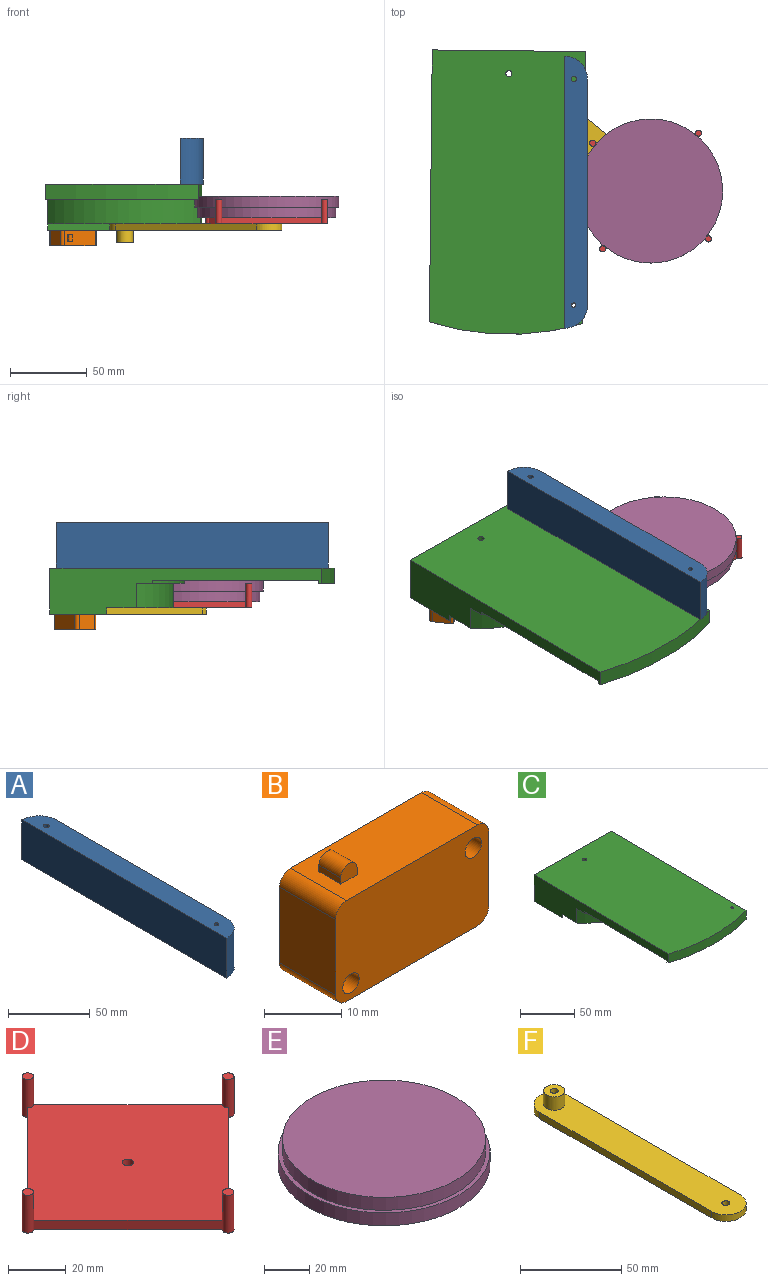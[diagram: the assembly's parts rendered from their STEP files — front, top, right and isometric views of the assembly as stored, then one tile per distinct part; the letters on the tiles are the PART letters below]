
ASSEMBLY  parts=6 mates=5
PART A: 8 faces, bbox 15x177.5x30 mm
  f0: cylinder r=15mm len=30mm, axis (0,0,-1), area 706.9mm2, adj f1,f4,f6,f7
  f1: plane 147.52x30mm, normal (1,0,0), area 4425.6mm2, adj f0,f2,f6,f7
  f2: cylinder r=15mm len=30mm, axis (0,0,-1), area 706.9mm2, adj f1,f4,f6,f7
  f3: cylinder r=1.5mm len=30mm, axis (0,0,-1), area 282.7mm2, adj f6,f7
  f4: plane 177.52x30mm, normal (-1,0,0), area 5325.6mm2, adj f0,f2,f6,f7
  f5: cylinder r=1.76mm len=30mm, axis (0,0,-1), area 331mm2, adj f6,f7
  f6: plane 177.52x15mm, normal (0,0,1), area 2549.5mm2, adj f0,f1,f2,f3,f4,f5
  f7: plane 177.52x15mm, normal (0,0,-1), area 2549.5mm2, adj f0,f1,f2,f3,f4,f5
PART B: 17 faces, bbox 28x10.3x18.5 mm
  f0: plane 24x10.3mm, normal (0,0,1), area 235.2mm2, adj f6,f7,f8,f9,f11,f12,f13,f16
  f1: plane 12x10.3mm, normal (-1,0,0), area 123.6mm2, adj f6,f7,f13,f14
  f2: plane 24x10.3mm, normal (0,0,-1), area 247.2mm2, adj f6,f7,f14,f15
  f3: cylinder r=1.5mm len=10.3mm, axis (0,1,0), area 97.1mm2, adj f6,f7
  f4: plane 12x10.3mm, normal (1,0,0), area 123.6mm2, adj f6,f7,f15,f16
  f5: cylinder r=1.5mm len=10.3mm, axis (0,1,0), area 97.1mm2, adj f6,f7
  f6: plane 28x16mm, normal (0,-1,0), area 430.4mm2, adj f0,f1,f2,f3,f4,f5,f13,f14
  f7: plane 28x16mm, normal (0,1,0), area 430.4mm2, adj f0,f1,f2,f3,f4,f5,f13,f14
  f8: plane 4x1mm, normal (-1,0,0), area 4mm2, adj f0,f10,f11,f12
  f9: plane 4x1mm, normal (1,0,0), area 4mm2, adj f0,f10,f11,f12
  f10: cylinder r=1.5mm len=4mm, axis (0,1,0), area 18.8mm2, adj f8,f9,f11,f12
  f11: plane 3x2.5mm, normal (0,-1,0), area 6.5mm2, adj f0,f8,f9,f10
  f12: plane 3x2.5mm, normal (0,1,0), area 6.5mm2, adj f0,f8,f9,f10
  f13: cylinder r=2mm len=10.3mm, axis (0,-1,0), area 32.4mm2, adj f0,f1,f6,f7
  f14: cylinder r=2mm len=10.3mm, axis (0,1,0), area 32.4mm2, adj f1,f2,f6,f7
  f15: cylinder r=2mm len=10.3mm, axis (0,-1,0), area 32.4mm2, adj f2,f4,f6,f7
  f16: cylinder r=2mm len=10.3mm, axis (0,1,0), area 32.4mm2, adj f0,f4,f6,f7
PART C: 18 faces, bbox 101.8x185.5x30 mm
  f0: plane 99.99x30mm, normal (0.01,1,0), area 3000mm2, adj f1,f3,f7,f17
  f1: plane 177.42x30mm, normal (-1,0.01,0), area 2606.2mm2, adj f0,f2,f6,f7,f8,f9,f10,f11
  f2: cylinder r=170mm len=99.99mm, axis (0,0,1), area 1015mm2, adj f1,f3,f7,f13
  f3: plane 177.52x30mm, normal (1,-0.01,0), area 2607.5mm2, adj f0,f2,f6,f7,f8,f9,f10,f11
  f4: cylinder r=2mm len=26mm, axis (0,0,1), area 326.7mm2, adj f7,f9
  f5: cylinder r=1.25mm len=8mm, axis (0,0,1), area 62.8mm2, adj f6,f7
  f6: plane 116.87x101.12mm, normal (0,0,-1), area 9973.8mm2, adj f1,f3,f5,f10,f12
  f7: plane 185.52x101.84mm, normal (0,0,1), area 18234.1mm2, adj f0,f1,f2,f3,f4,f5
  f8: cylinder r=65mm len=99.99mm, axis (0,0,1), area 1825.5mm2, adj f1,f3,f9,f11
  f9: plane 100.21x75.55mm, normal (0,0,-1), area 5312.2mm2, adj f1,f3,f4,f8,f14,f15,f16
  f10: cylinder r=72mm len=99.99mm, axis (0,0,1), area 221.1mm2, adj f1,f3,f6,f11
  f11: plane 100.1x31.18mm, normal (0,0,-1), area 785.2mm2, adj f1,f3,f8,f10
  f12: cylinder r=168mm len=99.99mm, axis (0,0,1), area 203.1mm2, adj f1,f3,f6,f13
  f13: plane 100.02x10.19mm, normal (0,0,-1), area 203mm2, adj f1,f2,f3,f12
  f14: plane 46.89x31.11mm, normal (-0.55,-0.83,0), area 225.1mm2, adj f3,f9,f15,f17
  f15: cylinder r=10.55mm len=11.06mm, axis (0,0,1), area 49.4mm2, adj f9,f14,f16,f17
  f16: plane 42.06x27.9mm, normal (0.55,-0.83,0), area 201.9mm2, adj f1,f9,f15,f17
  f17: plane 100.38x36.94mm, normal (0,0,-1), area 1959.9mm2, adj f0,f1,f3,f14,f15,f16
PART D: 15 faces, bbox 102x102x16 mm
  f0: plane 46.17x46.17mm, normal (0.71,0.71,0), area 261.2mm2, adj f5,f6,f9,f11
  f1: plane 46.17x46.17mm, normal (-0.71,0.71,0), area 261.2mm2, adj f5,f6,f11,f13
  f2: plane 46.17x46.17mm, normal (-0.71,-0.71,0), area 261.2mm2, adj f5,f6,f7,f13
  f3: cylinder r=2mm len=4mm, axis (0,0,-1), area 50.3mm2, adj f5,f6
  f4: plane 46.17x46.17mm, normal (0.71,-0.71,0), area 261.2mm2, adj f5,f6,f7,f9
  f5: plane 95.17x95.17mm, normal (0,0,1), area 4776.9mm2, adj f0,f1,f2,f3,f4,f7,f9,f11
  f6: plane 102x102mm, normal (0,0,-1), area 4827.1mm2, adj f0,f1,f2,f3,f4,f7,f9,f11
  f7: cylinder r=2mm len=16mm, axis (0,0,-1), area 188.5mm2, adj f2,f4,f5,f6,f8
  f8: plane 4x4mm, normal (0,0,1), area 12.6mm2, adj f7
  f9: cylinder r=2mm len=16mm, axis (0,0,-1), area 188.5mm2, adj f0,f4,f5,f6,f10
  f10: plane 4x4mm, normal (0,0,1), area 12.6mm2, adj f9
  f11: cylinder r=2mm len=16mm, axis (0,0,-1), area 188.5mm2, adj f0,f1,f5,f6,f12
  f12: plane 4x4mm, normal (0,0,1), area 12.6mm2, adj f11
  f13: cylinder r=2mm len=16mm, axis (0,0,-1), area 188.5mm2, adj f1,f2,f5,f6,f14
  f14: plane 4x4mm, normal (0,0,1), area 12.6mm2, adj f13
PART E: 5 faces, bbox 94x94x14 mm
  f0: cylinder r=47mm len=94mm, axis (0,0,-1), area 2067.2mm2, adj f1,f2
  f1: plane 94x94mm, normal (0,0,1), area 578.1mm2, adj f0,f3
  f2: plane 94x94mm, normal (0,0,-1), area 6939.8mm2, adj f0
  f3: cylinder r=45mm len=90mm, axis (0,0,-1), area 1979.2mm2, adj f1,f4
  f4: plane 90x90mm, normal (0,0,1), area 6361.7mm2, adj f3
PART F: 10 faces, bbox 20x140x12 mm
  f0: cylinder r=10mm len=20mm, axis (0,0,-1), area 125.7mm2, adj f1,f4,f6,f7
  f1: plane 120x4mm, normal (-1,0,0), area 480mm2, adj f0,f2,f6,f7
  f2: cylinder r=10mm len=20mm, axis (0,0,-1), area 125.7mm2, adj f1,f4,f6,f7
  f3: cylinder r=2mm len=4mm, axis (0,0,-1), area 50.3mm2, adj f6,f7
  f4: plane 120x4mm, normal (1,0,0), area 480mm2, adj f0,f2,f6,f7
  f5: cylinder r=2mm len=12mm, axis (0,0,-1), area 150.8mm2, adj f7,f9
  f6: plane 140x20mm, normal (0,0,1), area 2613.1mm2, adj f0,f1,f2,f3,f4,f8
  f7: plane 140x20mm, normal (0,0,-1), area 2689mm2, adj f0,f1,f2,f3,f4,f5
  f8: cylinder r=5.31mm len=10.62mm, axis (0,0,-1), area 266.8mm2, adj f6,f9
  f9: plane 10.62x10.62mm, normal (0,0,1), area 75.9mm2, adj f5,f8
PLACE A t=(-333.75,-1.49,-28.42)mm
PLACE B rot(axis=(0.92,0.28,0.28),94.8deg) t=(-208.68,-186.14,-63.57)mm
PLACE C t=(-143.75,1.51,-28.42)mm fixed
PLACE D rot(axis=(0,0,1),140.4deg) t=(-211.59,-298.79,-54.42)mm
PLACE E rot(axis=(-0.94,0.34,0),180deg) t=(-125.8,-311.99,-36.42)mm
PLACE F rot(axis=(-0.43,0.9,0),180deg) t=(-365.93,-42.17,-54.42)mm
MATE fastened F.f2 <-> D.f3  axis (0,0,1) through (-125.8,-311.99,-54.42)mm
MATE fastened A.f3 <-> C.f5  axis (0,0,-1) through (-175.99,-386.54,-28.42)mm
MATE fastened B.f0 <-> C.f16  axis (0.55,-0.83,0) through (-247.62,-242.97,-58.42)mm
MATE fastened E.f3 <-> D.f3  axis (0,0,-1) through (-125.8,-311.99,-50.42)mm
MATE revolute F.f0 <-> C.f2  axis (0,0,1) through (-218.27,-235.5,-54.42)mm
